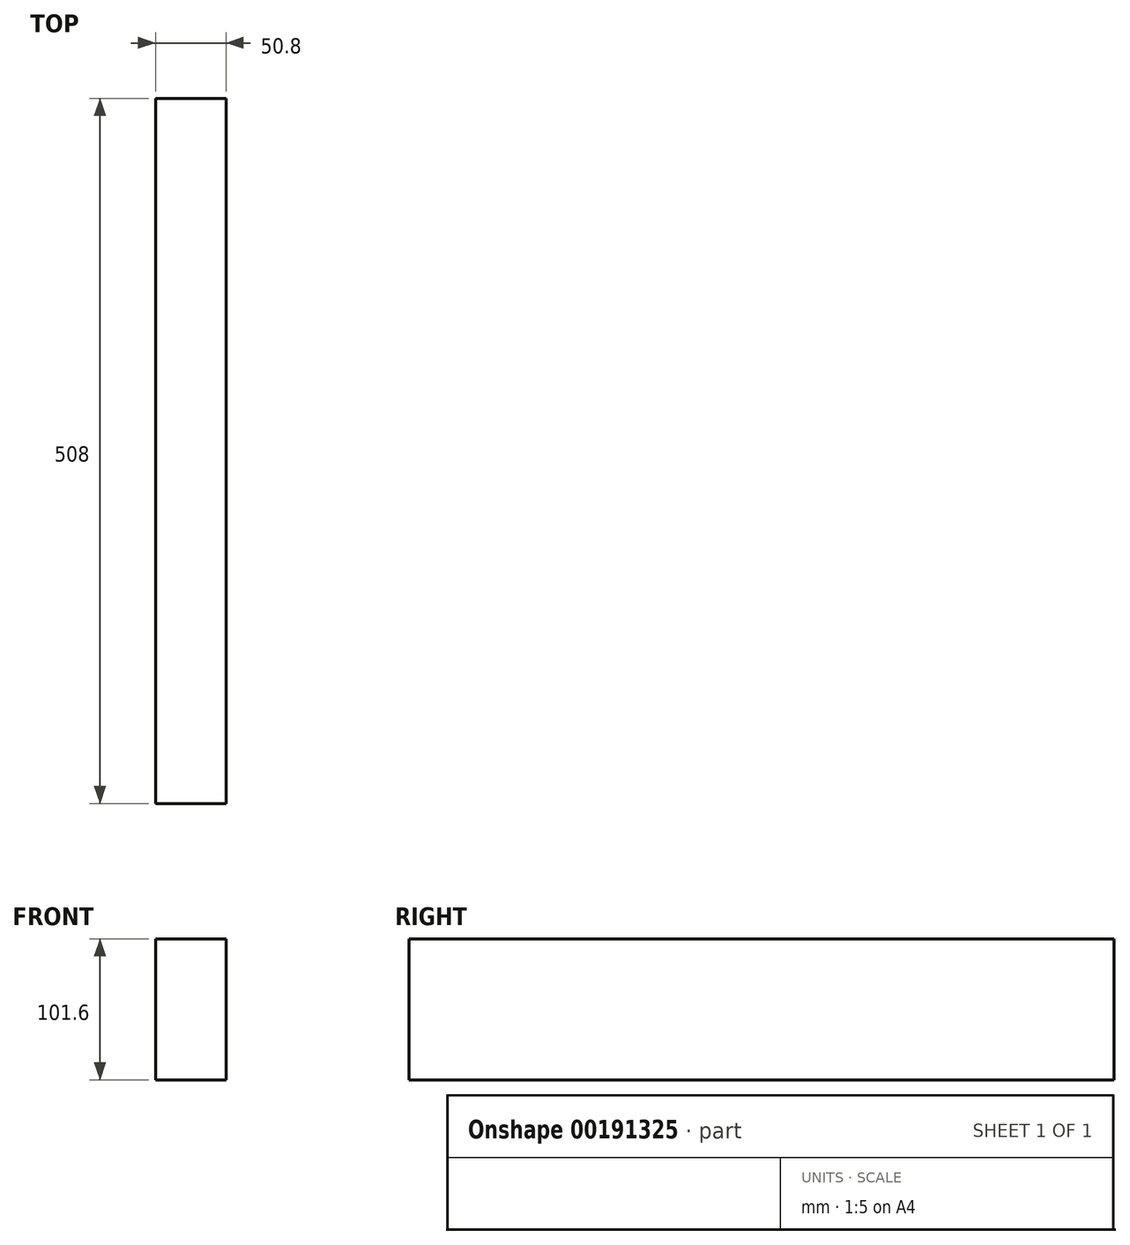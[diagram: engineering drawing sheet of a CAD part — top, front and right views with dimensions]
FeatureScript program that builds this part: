
annotation { "Feature Type Name" : "Feature", "Feature Type Description" : "" }
export const myFeature = defineFeature(function(context is Context, id is Id, definition is map)
    precondition{}
    {
        {
            var Q0;
            Q0=qCreatedBy(makeId("Front.planeOp"),FACE);
            var sketch = newSketch(context, id + "F0", { "sketchPlane" : qUnion([Q0])});
            skLineSegment(sketch, "E0.bottom", {"start": v(-25.4, 50.8) * mm, "end": v(25.4, 50.8) * mm});
            skLineSegment(sketch, "E0.top", {"start": v(-25.4, -50.8) * mm, "end": v(25.4, -50.8) * mm});
            skLineSegment(sketch, "E0.left", {"start": v(-25.4, 50.8) * mm, "end": v(-25.4, -50.8) * mm});
            skLineSegment(sketch, "E0.right", {"start": v(25.4, 50.8) * mm, "end": v(25.4, -50.8) * mm});
            skLineSegment(sketch, "E1", {"start": v(-25.4, 50.8) * mm, "end": v(25.4, -50.8) * mm, "construction": true});
            skSolve(sketch);
        }
        {
            var Q0;
            Q0=makeQuery(id+"F0.imprint","IMPRINT",FACE,{"disambiguationData":[TD([[makeQuery(id+"F0.imprint","IMPRINT",EDGE,{"derivedFrom":sQuery(id+"F0.wireOp",EDGE,"E0.bottom")}),-1.0]])]});
            extrude(context, id + "F1", {"entities" : qUnion([Q0]), "depth" : 508 * mm});
        }
    });
